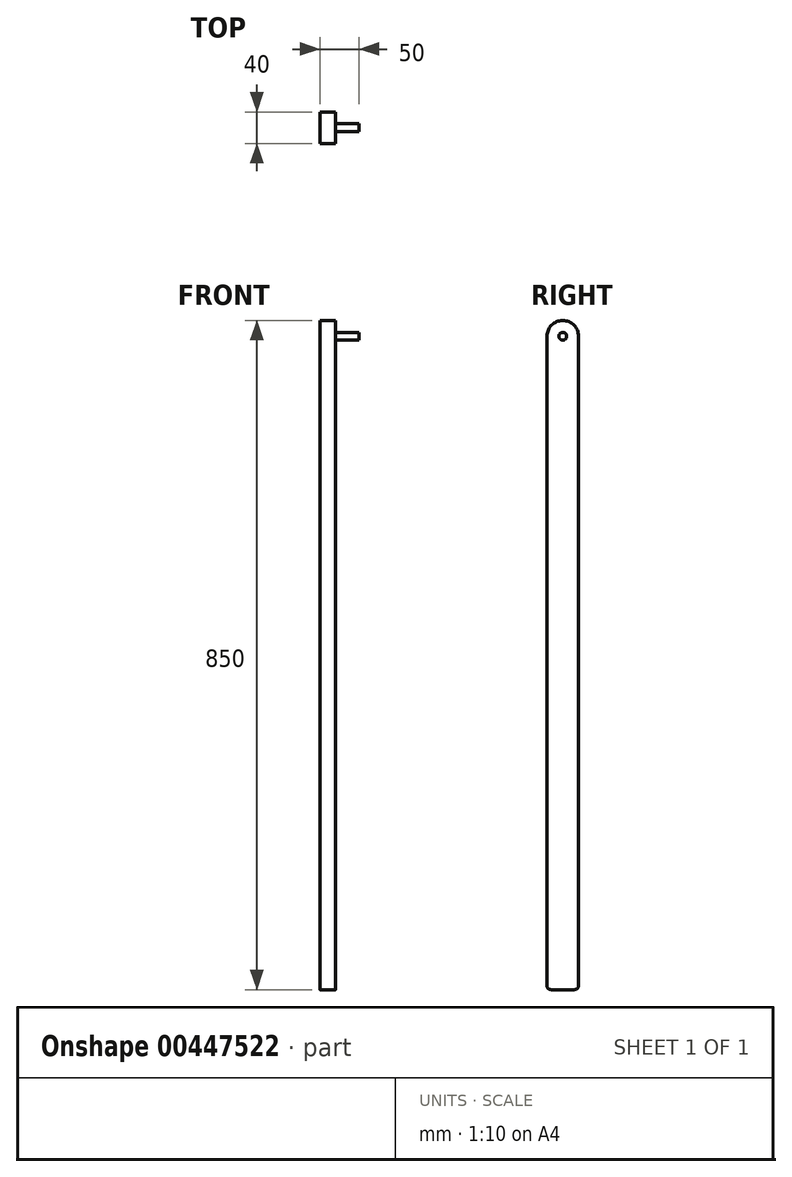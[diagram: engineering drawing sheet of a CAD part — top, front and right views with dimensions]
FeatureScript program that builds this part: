
annotation { "Feature Type Name" : "Feature", "Feature Type Description" : "" }
export const myFeature = defineFeature(function(context is Context, id is Id, definition is map)
    precondition{}
    {
        {
            var Q0;
            Q0=qCreatedBy(makeId("Right.planeOp"),FACE);
            var sketch = newSketch(context, id + "F0", { "sketchPlane" : qUnion([Q0])});
            skLineSegment(sketch, "E0.bottom", {"start": v(0, 425) * mm, "end": v(0, 425) * mm});
            skLineSegment(sketch, "E0.top", {"start": v(-15, -425) * mm, "end": v(15, -425) * mm});
            skLineSegment(sketch, "E0.left", {"start": v(-20, 405) * mm, "end": v(-20, -420) * mm});
            skLineSegment(sketch, "E0.right", {"start": v(20, 405) * mm, "end": v(20, -420) * mm});
            skPoint(sketch, "E0.middle", {"position": v(0, 0) * mm});
            skPoint(sketch, "E1.visualSharp", {"position": v(-20, -425) * mm});
            skArc(sketch, "E1.filletArc", {"start": v(-20, -420) * mm, "mid": v(-18.54, -423.54) * mm, "end": v(-15, -425) * mm});
            skPoint(sketch, "E2.visualSharp", {"position": v(20, -425) * mm});
            skArc(sketch, "E2.filletArc", {"start": v(15, -425) * mm, "mid": v(18.54, -423.54) * mm, "end": v(20, -420) * mm});
            skPoint(sketch, "E3.visualSharp", {"position": v(20, 425) * mm});
            skArc(sketch, "E3.filletArc", {"start": v(20, 405) * mm, "mid": v(14.14, 419.14) * mm, "end": v(0, 425) * mm});
            skPoint(sketch, "E4.visualSharp", {"position": v(-20, 425) * mm});
            skArc(sketch, "E4.filletArc", {"start": v(0, 425) * mm, "mid": v(-14.14, 419.14) * mm, "end": v(-20, 405) * mm});
            skCircle(sketch, "E5", {"center": v(0, 405) * mm, "radius": 4.99 * mm});
            skSolve(sketch);
        }
        {
            var Q0;
            Q0=makeQuery(id+"F0.imprint","IMPRINT",FACE,{"disambiguationData":[TD([[makeQuery(id+"F0.imprint","IMPRINT",EDGE,{"derivedFrom":sQuery(id+"F0.wireOp",EDGE,"E0.top")}),1.0]])]});
            extrude(context, id + "F1", {"entities" : qUnion([Q0]), "depth" : 20 * mm});
        }
        {
            var Q0;
            Q0=makeQuery(id+"F0.imprint","IMPRINT",FACE,{"disambiguationData":[TD([[makeQuery(id+"F0.imprint","IMPRINT",EDGE,{"derivedFrom":sQuery(id+"F0.wireOp",EDGE,"E5")}),1.0]])]});
            extrude(context, id + "F2", {"entities" : qUnion([Q0]), "operationType" : NewBodyOperationType.ADD, "depth" : 50 * mm});
        }
    });
